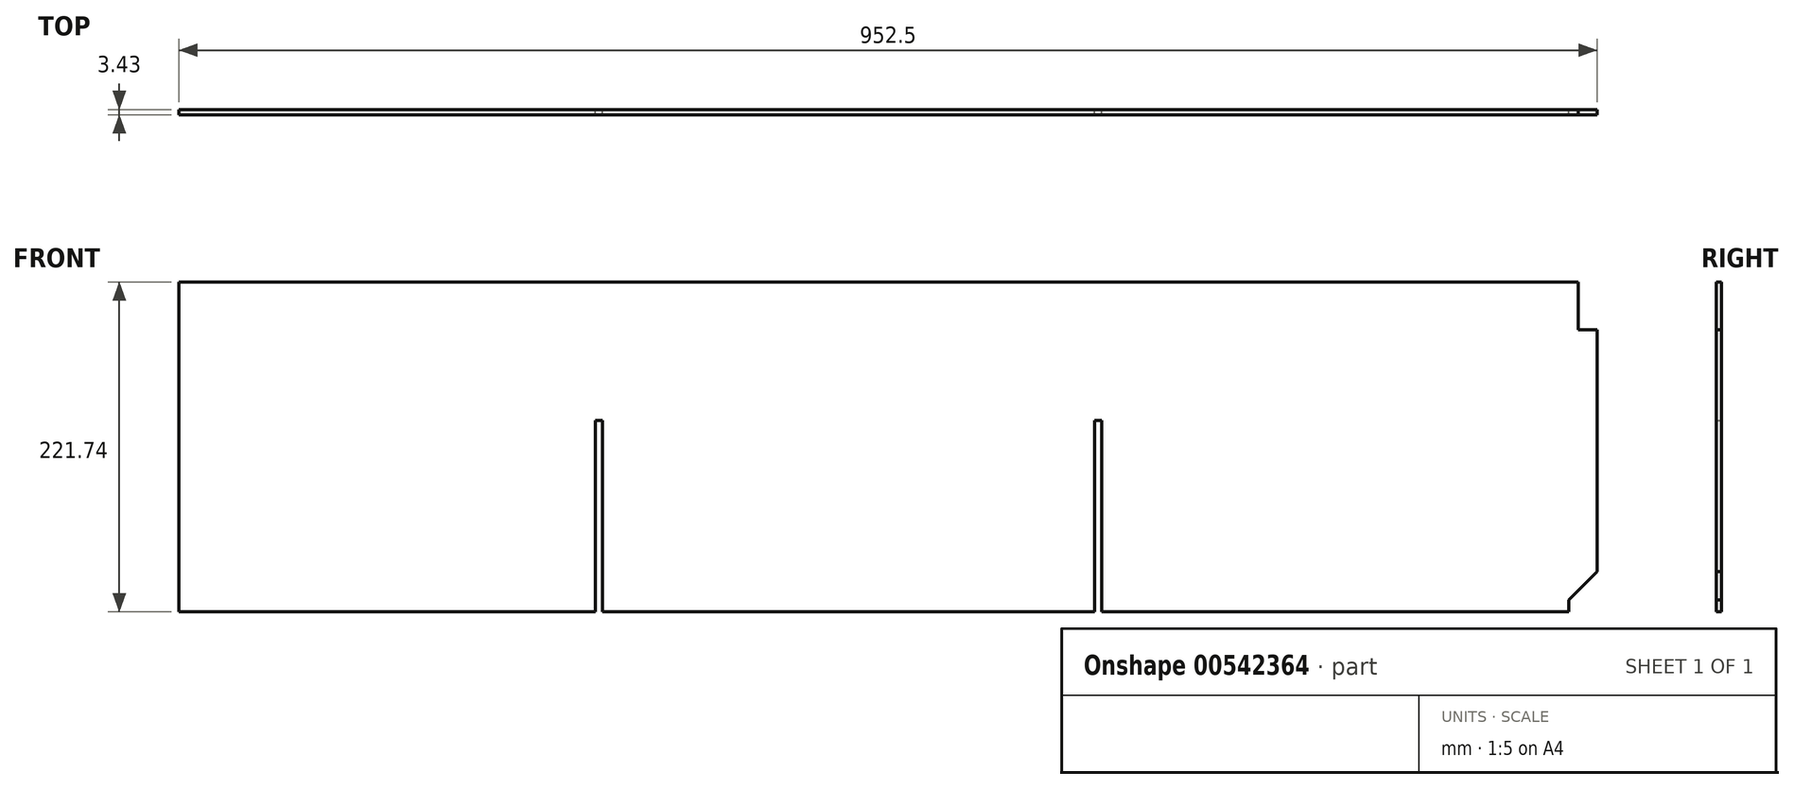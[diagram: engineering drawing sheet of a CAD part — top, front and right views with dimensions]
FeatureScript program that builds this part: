
annotation { "Feature Type Name" : "Feature", "Feature Type Description" : "" }
export const myFeature = defineFeature(function(context is Context, id is Id, definition is map)
    precondition{}
    {
        {
            var Q0;
            Q0=qCreatedBy(makeId("Front.planeOp"),FACE);
            var sketch = newSketch(context, id + "F0", { "sketchPlane" : qUnion([Q0])});
            skLineSegment(sketch, "E0.left", {"start": v(-476.25, -110.87) * mm, "end": v(-476.25, 110.87) * mm});
            skPoint(sketch, "E0.middle", {"position": v(0, 0) * mm});
            skLineSegment(sketch, "E1.top", {"start": v(-191.93, 17.72) * mm, "end": v(-196.7, 17.72) * mm});
            skLineSegment(sketch, "E1.left", {"start": v(-191.93, -110.87) * mm, "end": v(-191.93, 17.72) * mm});
            skLineSegment(sketch, "E1.right", {"start": v(-196.7, -110.87) * mm, "end": v(-196.7, 17.72) * mm});
            skPoint(sketch, "E1.middle", {"position": v(-194.3, -46.58) * mm});
            skLineSegment(sketch, "E2.top", {"start": v(143.35, 17.72) * mm, "end": v(138.59, 17.72) * mm});
            skLineSegment(sketch, "E2.left", {"start": v(143.35, -110.87) * mm, "end": v(143.35, 17.72) * mm});
            skLineSegment(sketch, "E2.right", {"start": v(138.59, -110.87) * mm, "end": v(138.59, 17.72) * mm});
            skPoint(sketch, "E2.middle", {"position": v(140.97, -46.58) * mm});
            skLineSegment(sketch, "E3.top", {"start": v(476.25, 78.8) * mm, "end": v(463.55, 78.8) * mm});
            skLineSegment(sketch, "E3.right", {"start": v(463.55, 110.87) * mm, "end": v(463.55, 78.8) * mm});
            skLineSegment(sketch, "E4.right", {"start": v(457.2, -110.87) * mm, "end": v(457.2, -102.7) * mm});
            skLineSegment(sketch, "E5", {"start": v(457.2, -102.7) * mm, "end": v(476.25, -83.64) * mm});
            skLineSegment(sketch, "E6", {"start": v(-476.25, -110.87) * mm, "end": v(-196.7, -110.87) * mm});
            skLineSegment(sketch, "E7", {"start": v(-191.93, -110.87) * mm, "end": v(138.59, -110.87) * mm});
            skLineSegment(sketch, "E8", {"start": v(457.2, -110.87) * mm, "end": v(143.35, -110.87) * mm});
            skLineSegment(sketch, "E9", {"start": v(476.25, -83.64) * mm, "end": v(476.25, 78.8) * mm});
            skLineSegment(sketch, "E10", {"start": v(463.55, 110.87) * mm, "end": v(-476.25, 110.87) * mm});
            skSolve(sketch);
        }
        {
            var Q0;
            Q0=makeQuery(id+"F0.imprint","IMPRINT",FACE,{"disambiguationData":[TD([[makeQuery(id+"F0.imprint","IMPRINT",EDGE,{"derivedFrom":sQuery(id+"F0.wireOp",EDGE,"E0.left")}),-1.0]])]});
            extrude(context, id + "F1", {"entities" : qUnion([Q0]), "depth" : 3.43 * mm, "offsetDistance" : 25.4 * mm});
        }
    });
